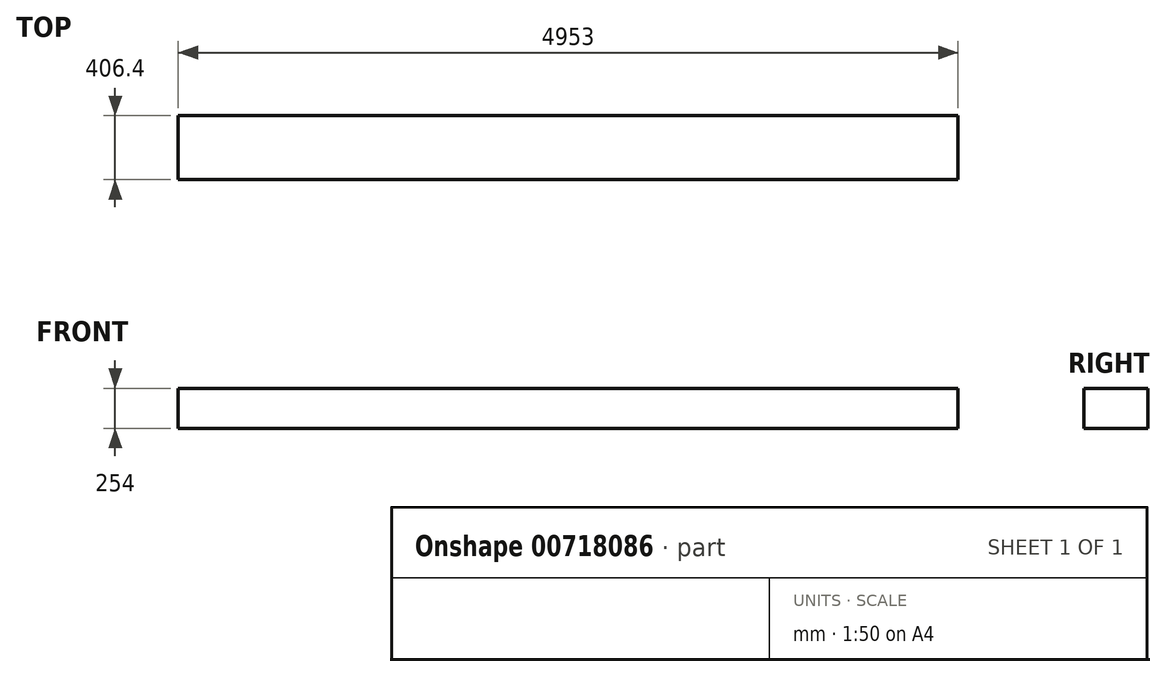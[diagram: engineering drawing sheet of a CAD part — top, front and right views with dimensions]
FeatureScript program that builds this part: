
annotation { "Feature Type Name" : "Feature", "Feature Type Description" : "" }
export const myFeature = defineFeature(function(context is Context, id is Id, definition is map)
    precondition{}
    {
        {
            var Q0;
            Q0=qCreatedBy(makeId("Right.planeOp"),FACE);
            var sketch = newSketch(context, id + "F0", { "sketchPlane" : qUnion([Q0])});
            skLineSegment(sketch, "E0.bottom", {"start": v(203.2, -127) * mm, "end": v(-203.2, -127) * mm});
            skLineSegment(sketch, "E0.top", {"start": v(203.2, 127) * mm, "end": v(-203.2, 127) * mm});
            skLineSegment(sketch, "E0.left", {"start": v(203.2, -127) * mm, "end": v(203.2, 127) * mm});
            skLineSegment(sketch, "E0.right", {"start": v(-203.2, -127) * mm, "end": v(-203.2, 127) * mm});
            skPoint(sketch, "E0.middle", {"position": v(0, 0) * mm});
            skSolve(sketch);
        }
        {
            var Q0;
            Q0 = qSketchRegion(id + "F0", true);
            extrude(context, id + "F1", {"entities" : qUnion([Q0]), "depth" : 4953 * mm, "offsetDistance" : 25.4 * mm, "hasDraft" : true, "draftAngle" : 0 * degree});
        }
    });
